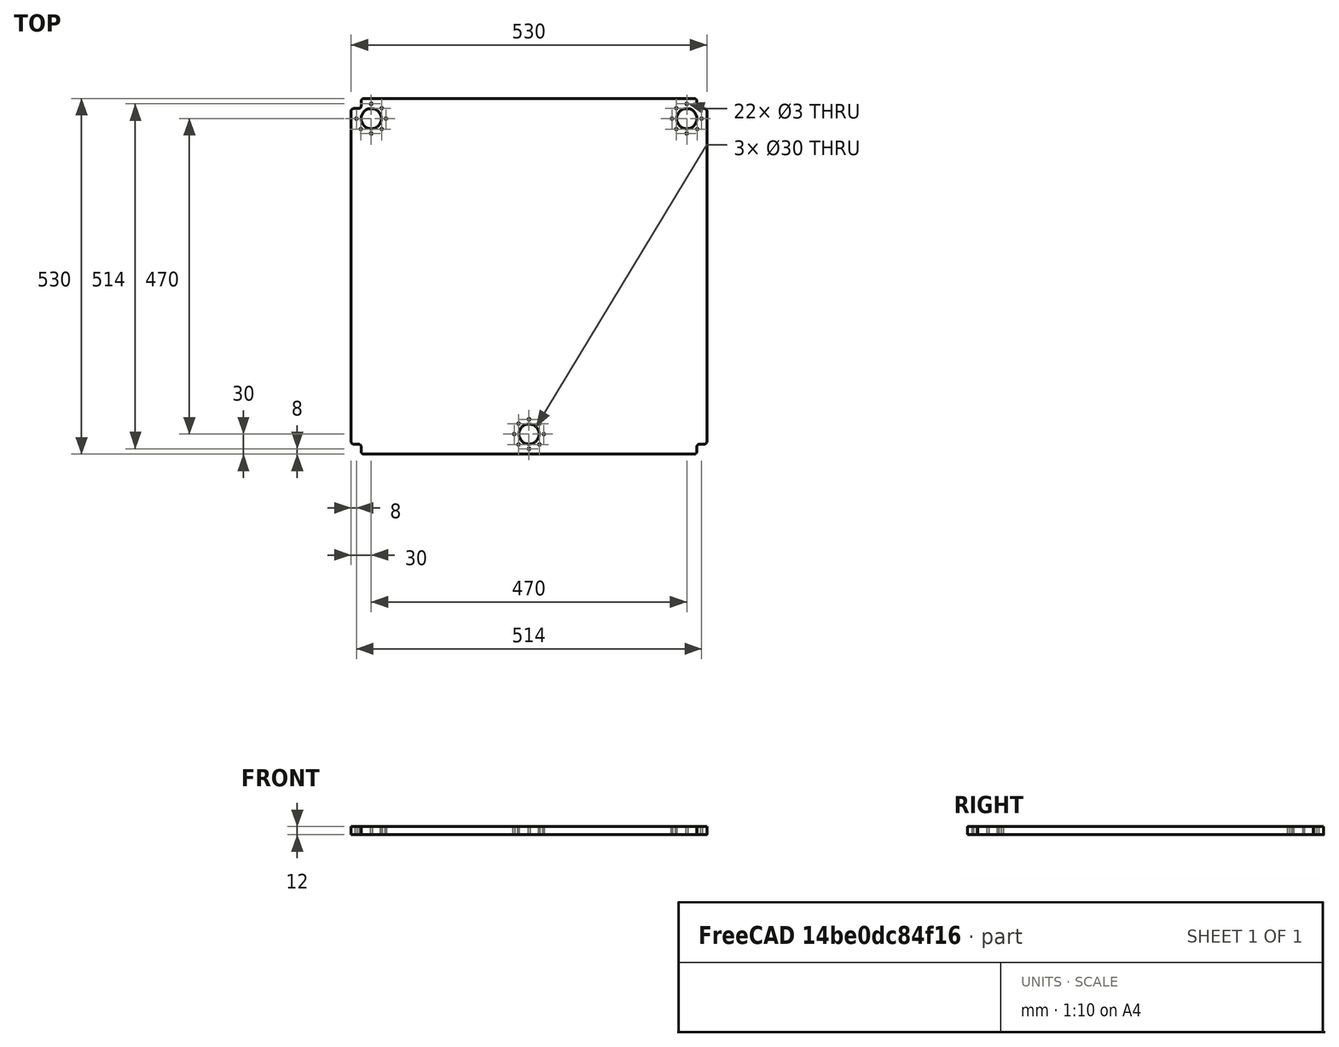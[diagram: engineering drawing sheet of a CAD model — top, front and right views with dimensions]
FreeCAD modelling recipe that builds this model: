
FCSTD DOCUMENT  (FreeCAD 0.19R)
Label: plateau_horizontal
License: All rights reserved
LicenseURL: http://en.wikipedia.org/wiki/All_rights_reserved
objects: TechDraw::DrawViewDimension×6, Sketcher::SketchObject×4, PartDesign::Pocket×3, PartDesign::Line×3, PartDesign::PolarPattern×3, TechDraw::DrawSVGTemplate×2, TechDraw::DrawPage×2, PartDesign::Pad×1, PartDesign::CoordinateSystem×1, PartDesign::Body×1, TechDraw::DrawViewPart×1
note: 20 computed .brp shape members not serialized (recipe doc carries the construction recipe); baked Part::Feature solids carry a one-line shape summary decoded from their .brp

FEATURE [Sketcher::SketchObject] Sketch
  FullyConstrained = true
  MapMode = 5
  Support = -> [XY_Plane]
  sketch-geometry (27):
    g0: Circle CenterX=0 CenterY=-235 CenterZ=0 NormalX=0 NormalY=0 NormalZ=1 AngleXU=0 Radius=15
    g1: Circle CenterX=-235 CenterY=235 CenterZ=0 NormalX=0 NormalY=0 NormalZ=1 AngleXU=0 Radius=15
    g2: Circle CenterX=235 CenterY=235 CenterZ=0 NormalX=0 NormalY=0 NormalZ=1 AngleXU=0 Radius=15
    g3: LineSegment StartX=-261 StartY=250 StartZ=0 EndX=-254 EndY=250 EndZ=0
    g4: LineSegment StartX=-250 StartY=254 StartZ=0 EndX=-250 EndY=261 EndZ=0
    g5: LineSegment StartX=-246 StartY=265 StartZ=0 EndX=246 EndY=265 EndZ=0
    g6: LineSegment StartX=250 StartY=261 StartZ=0 EndX=250 EndY=254 EndZ=0
    g7: LineSegment StartX=254 StartY=250 StartZ=0 EndX=261 EndY=250 EndZ=0
    g8: LineSegment StartX=265 StartY=246 StartZ=0 EndX=265 EndY=-246 EndZ=0
    g9: LineSegment StartX=261 StartY=-250 StartZ=0 EndX=254 EndY=-250 EndZ=0
    g10: LineSegment StartX=250 StartY=-254 StartZ=0 EndX=250 EndY=-261 EndZ=0
    g11: LineSegment StartX=246 StartY=-265 StartZ=0 EndX=-246 EndY=-265 EndZ=0
    g12: LineSegment StartX=-250 StartY=-261 StartZ=0 EndX=-250 EndY=-254 EndZ=0
    g13: LineSegment StartX=-254 StartY=-250 StartZ=0 EndX=-261 EndY=-250 EndZ=0
    g14: LineSegment StartX=-265 StartY=-246 StartZ=0 EndX=-265 EndY=246 EndZ=0
    g15: ArcOfCircle CenterX=-246 CenterY=261 CenterZ=0 NormalX=0 NormalY=0 NormalZ=1 AngleXU=0 Radius=4 StartAngle=1.5708 EndAngle=3.14159
    g16: ArcOfCircle CenterX=-254 CenterY=254 CenterZ=0 NormalX=0 NormalY=0 NormalZ=1 AngleXU=0 Radius=4 StartAngle=4.71239 EndAngle=6.28319
    g17: ArcOfCircle CenterX=-261 CenterY=246 CenterZ=0 NormalX=0 NormalY=0 NormalZ=1 AngleXU=0 Radius=4 StartAngle=1.5708 EndAngle=3.14159
    g18: ArcOfCircle CenterX=-261 CenterY=-246 CenterZ=0 NormalX=0 NormalY=0 NormalZ=1 AngleXU=0 Radius=4 StartAngle=3.14159 EndAngle=4.71239
    g19: ArcOfCircle CenterX=-254 CenterY=-254 CenterZ=0 NormalX=0 NormalY=0 NormalZ=1 AngleXU=0 Radius=4 StartAngle=1.5e-15 EndAngle=1.5708
    g20: ArcOfCircle CenterX=-246 CenterY=-261 CenterZ=0 NormalX=0 NormalY=0 NormalZ=1 AngleXU=0 Radius=4 StartAngle=3.14159 EndAngle=4.71239
    g21: ArcOfCircle CenterX=246 CenterY=-261 CenterZ=0 NormalX=0 NormalY=0 NormalZ=1 AngleXU=0 Radius=4 StartAngle=4.71239 EndAngle=6.28319
    g22: ArcOfCircle CenterX=254 CenterY=-254 CenterZ=0 NormalX=0 NormalY=0 NormalZ=1 AngleXU=0 Radius=4 StartAngle=1.5708 EndAngle=3.14159
    g23: ArcOfCircle CenterX=261 CenterY=-246 CenterZ=0 NormalX=0 NormalY=0 NormalZ=1 AngleXU=0 Radius=4 StartAngle=4.71239 EndAngle=6.28319
    g24: ArcOfCircle CenterX=261 CenterY=246 CenterZ=0 NormalX=0 NormalY=0 NormalZ=1 AngleXU=0 Radius=4 StartAngle=-1.8e-15 EndAngle=1.5708
    g25: ArcOfCircle CenterX=246 CenterY=261 CenterZ=0 NormalX=0 NormalY=0 NormalZ=1 AngleXU=0 Radius=4 StartAngle=-2.7e-15 EndAngle=1.5708
    g26: ArcOfCircle CenterX=254 CenterY=254 CenterZ=0 NormalX=0 NormalY=0 NormalZ=1 AngleXU=0 Radius=4 StartAngle=3.14159 EndAngle=4.71239
  constraints (62):
    c: PointOnObject(g0,g-2)
    c: Radius(g0) = 15
    c: Radius(g1) = 15
    c: Radius(g2) = 15
    c: Symmetric(g2,g1,g-2)
    c: Horizontal(g3)
    c: Vertical(g10)
    c: Horizontal(g11)
    c: Vertical(g12)
    c: Horizontal(g13)
    c: Vertical(g14)
    c: Tangent(g4,g15) = 1.5708
    c: Tangent(g5,g15) = 1.5708
    c: Tangent(g3,g16) = -1.5708
    c: Tangent(g4,g16) = -1.5708
    c: Tangent(g14,g17) = 1.5708
    c: Tangent(g3,g17) = 1.5708
    c: Tangent(g13,g18) = 1.5708
    c: Tangent(g14,g18) = 1.5708
    c: Tangent(g13,g19) = -1.5708
    c: Tangent(g12,g19) = -1.5708
    c: Tangent(g12,g20) = 1.5708
    c: Tangent(g11,g20) = 1.5708
    c: Tangent(g11,g21) = 1.5708
    c: Tangent(g10,g21) = 1.5708
    c: Tangent(g10,g22) = -1.5708
    c: Tangent(g9,g22) = -1.5708
    c: Tangent(g7,g24) = 1.5708
    c: Tangent(g8,g24) = 1.5708
    c: Tangent(g5,g25) = 1.5708
    c: Tangent(g6,g25) = 1.5708
    c: Tangent(g7,g26) = -1.5708
    c: Tangent(g6,g26) = -1.5708
    c: Symmetric(g5,g5,g-2)
    c: Symmetric(g4,g6,g-2)
    c: Symmetric(g7,g3,g-2)
    c: Symmetric(g7,g3,g-2)
    c: Vertical(g6)
    c: DistanceY(g0,g-1) = 235
    c: DistanceX(g1,g2) = 470
    c: DistanceY(g-1,g1) = 235
    c: DistanceY(g7,g5) = 15
    c: DistanceY(g-1,g7) = 250
    c: DistanceX(g-1,g6) = 250
    c: DistanceX(g6,g8) = 15
    c: Symmetric(g4,g12,g-1)
    c: Symmetric(g11,g5,g-1)
    c: Tangent(g23,g9) = 1.5708
    c: Tangent(g8,g23) = 1.5708
    c: Horizontal(g9)
    c: Vertical(g8)
    c: Radius(g22) = 4
    c: Radius(g21) = 4
    c: Radius(g23) = 4
    c: Radius(g18) = 4
    c: Radius(g19) = 4
    c: Radius(g20) = 4
    c: Radius(g24) = 4
    c: Radius(g26) = 4
    c: DistanceY(g11,g9) = 15
    c: DistanceX(g10,g8) = 15
    c: DistanceX(g14,g12) = 15
FEATURE [PartDesign::Pad] Pad
  Direction = (1,1,1)
  Length = 12
  Length2 = 100
  Profile = -> Sketch
  Type = 0
FEATURE [Sketcher::SketchObject] Sketch001
  ExternalGeometry = -> [Pad]
  FullyConstrained = true
  MapMode = 5
  Placement = pos=(0,0,12) rot=(0,0,1;0rad)
  Support = -> [Pad]
  sketch-geometry (2):
    g0: Circle CenterX=235 CenterY=257 CenterZ=0 NormalX=0 NormalY=0 NormalZ=1 AngleXU=0 Radius=1.5
    g1: LineSegment StartX=235 StartY=257 StartZ=0 EndX=235 EndY=235 EndZ=0
  constraints (5):
    c: Coincident(g1,g0)
    c: Coincident(g1,g-3)
    c: Vertical(g1)
    c: Radius(g0) = 1.5
    c: DistanceY(g1,g1) = 22
FEATURE [PartDesign::Pocket] Pocket
  BaseFeature = -> Pad
  Length = 5
  Length2 = 100
  Profile = -> Sketch001
  Type = 1
FEATURE [PartDesign::Line] DatumLine
  AttacherType = Attacher::AttachEngineLine
  Length = 20
  MapMode = 42
  Placement = pos=(235,235,0) rot=(0,0,1;0rad)
  ResizeMode = 0
  Support = -> [Pocket]
FEATURE [PartDesign::PolarPattern] PolarPattern
  Angle = 270
  Axis = -> DatumLine
  BaseFeature = -> Pocket
  Occurrences = 7
  Originals = -> [Pocket]
FEATURE [Sketcher::SketchObject] Sketch002
  ExternalGeometry = -> [PolarPattern]
  FullyConstrained = true
  MapMode = 5
  Placement = pos=(0,0,12) rot=(0,0,1;0rad)
  Support = -> [PolarPattern]
  sketch-geometry (2):
    g0: Circle CenterX=-235 CenterY=257 CenterZ=0 NormalX=0 NormalY=0 NormalZ=1 AngleXU=0 Radius=1.5
    g1: LineSegment StartX=-235 StartY=257 StartZ=0 EndX=-235 EndY=235 EndZ=0
  constraints (5):
    c: Coincident(g1,g0)
    c: Coincident(g1,g-3)
    c: Vertical(g1)
    c: Radius(g0) = 1.5
    c: DistanceY(g1,g1) = 22
FEATURE [PartDesign::Pocket] Pocket001
  BaseFeature = -> PolarPattern
  Length = 5
  Length2 = 100
  Profile = -> Sketch002
  Type = 1
FEATURE [PartDesign::Line] DatumLine001
  AttacherType = Attacher::AttachEngineLine
  Length = 20
  MapMode = 42
  Placement = pos=(-235,235,0) rot=(0,0,1;0rad)
  ResizeMode = 0
  Support = -> [Pocket001]
FEATURE [PartDesign::PolarPattern] PolarPattern001
  Angle = 270
  Axis = -> DatumLine001
  BaseFeature = -> Pocket001
  Occurrences = 7
  Originals = -> [Pocket001]
  Reversed = true
FEATURE [Sketcher::SketchObject] Sketch003
  ExternalGeometry = -> [PolarPattern001]
  FullyConstrained = true
  MapMode = 5
  Placement = pos=(0,0,12) rot=(0,0,1;0rad)
  Support = -> [PolarPattern001]
  sketch-geometry (1):
    g0: Circle CenterX=0 CenterY=-213 CenterZ=0 NormalX=0 NormalY=0 NormalZ=1 AngleXU=0 Radius=1.5
  constraints (3):
    c: PointOnObject(g0,g-2)
    c: DistanceY(g-3,g0) = 22
    c: Radius(g0) = 1.5
FEATURE [PartDesign::Pocket] Pocket002
  BaseFeature = -> PolarPattern001
  Length = 5
  Length2 = 100
  Profile = -> Sketch003
  Type = 1
FEATURE [PartDesign::Line] DatumLine002
  AttacherType = Attacher::AttachEngineLine
  Length = 20
  MapMode = 42
  Placement = pos=(1e-16,-235,0) rot=(0,0,1;0rad)
  ResizeMode = 0
  Support = -> [Pocket002]
FEATURE [PartDesign::PolarPattern] PolarPattern002
  Angle = 360
  Axis = -> DatumLine002
  BaseFeature = -> Pocket002
  Occurrences = 8
  Originals = -> [Pocket002]
FEATURE [PartDesign::CoordinateSystem] Local_CS
  AttacherType = Attacher::AttachEngine3D
  MapMode = 2
FEATURE [PartDesign::Body] Body
  Group = -> [Sketch,Pad,Sketch001,Pocket,DatumLine,PolarPattern,Sketch002,Pocket001,DatumLine001,PolarPattern001,Sketch003,Pocket002,DatumLine002,PolarPattern002,Local_CS]
  Origin = -> Origin
  Tip = -> PolarPattern002
FEATURE [TechDraw::DrawSVGTemplate] Template
  EditableTexts = Designed_by_Name=Designed by Name; Drawing_number=Drawing number; FC-Date=Date; FC-SC=Scale; FC-SH=Sheet; FC-Title=Title; Subtitle=Subtitle; Weight=Weight
  Height = 210
  Orientation = 1
  Width = 297
FEATURE [TechDraw::DrawViewPart] View
  CoarseView = false
  Direction = (0,0,1)
  Focus = 100
  HardHidden = false
  IsoCount = 0
  IsoHidden = false
  IsoVisible = false
  LockPosition = false
  Perspective = false
  Rotation = 0
  Scale = 0.2
  ScaleType = 0
  SeamHidden = false
  SeamVisible = true
  SmoothHidden = false
  SmoothVisible = true
  Source = -> [Body]
  X = 84.1
  XDirection = (1,0,0)
  Y = 133
FEATURE [TechDraw::DrawViewDimension] Dimension
  Arbitrary = false
  ArbitraryTolerances = false
  EqualTolerance = true
  FormatSpec = %.0f
  FormatSpecTolerance = %+.0f
  Inverted = false
  LockPosition = false
  MeasureType = 1
  OverTolerance = 0
  References2D = -> [View]
  Rotation = 0
  Scale = 0.2
  ScaleType = 0
  TheoreticalExact = false
  Type = 1
  UnderTolerance = 0
  X = -0.625143
  Y = -61.4843
FEATURE [TechDraw::DrawSVGTemplate] Template001
  EditableTexts = Designed_by_Name=Designed by Name; Drawing_number=Drawing number; FC-Date=Date; FC-SC=Scale; FC-SH=Sheet; FC-Title=Title; Subtitle=Subtitle; Weight=Weight
  Height = 210
  Orientation = 1
  Width = 297
FEATURE [TechDraw::DrawPage] Page001
  KeepUpdated = true
  NextBalloonIndex = 1
  ProjectionType = 0
  Template = -> Template001
FEATURE [TechDraw::DrawViewDimension] Dimension001
  Arbitrary = false
  ArbitraryTolerances = false
  EqualTolerance = true
  FormatSpec = %.0f
  FormatSpecTolerance = %+.0f
  Inverted = false
  LockPosition = false
  MeasureType = 1
  OverTolerance = 0
  References2D = -> [View]
  Rotation = 0
  Scale = 0.2
  ScaleType = 0
  TheoreticalExact = false
  Type = 1
  UnderTolerance = 0
  X = -2.81314
  Y = -54.8634
FEATURE [TechDraw::DrawViewDimension] Dimension002
  Arbitrary = false
  ArbitraryTolerances = false
  EqualTolerance = true
  FormatSpec = %.0f
  FormatSpecTolerance = %+.0f
  Inverted = false
  LockPosition = false
  MeasureType = 1
  OverTolerance = 0
  References2D = -> [View]
  Rotation = 0
  Scale = 0.2
  ScaleType = 0
  TheoreticalExact = false
  Type = 2
  UnderTolerance = 0
  X = 61.264
  Y = -34.4529
FEATURE [TechDraw::DrawViewDimension] Dimension003
  Arbitrary = false
  ArbitraryTolerances = false
  EqualTolerance = true
  FormatSpec = %.0f
  FormatSpecTolerance = %+.0f
  Inverted = false
  LockPosition = false
  MeasureType = 1
  OverTolerance = 0
  References2D = -> [View]
  Rotation = 0
  Scale = 0.2
  ScaleType = 0
  TheoreticalExact = false
  Type = 2
  UnderTolerance = 0
  X = 57.1057
  Y = 64.6369
FEATURE [TechDraw::DrawViewDimension] Dimension004
  Arbitrary = false
  ArbitraryTolerances = false
  EqualTolerance = true
  FormatSpec = %.0f
  FormatSpecTolerance = %+.0f
  Inverted = false
  LockPosition = false
  MeasureType = 1
  OverTolerance = 0
  References2D = -> [View]
  Rotation = 0
  Scale = 0.2
  ScaleType = 0
  TheoreticalExact = false
  Type = 2
  UnderTolerance = 0
  X = -45.0277
  Y = 63.5988
FEATURE [TechDraw::DrawViewDimension] Dimension005
  Arbitrary = false
  ArbitraryTolerances = false
  EqualTolerance = true
  FormatSpec = %.0f
  FormatSpecTolerance = %+.0f
  Inverted = false
  LockPosition = false
  MeasureType = 1
  OverTolerance = 0
  References2D = -> [View]
  Rotation = 0
  Scale = 0.2
  ScaleType = 0
  TheoreticalExact = false
  Type = 1
  UnderTolerance = 0
  X = -2.73924
  Y = 37.2415
FEATURE [TechDraw::DrawPage] Page
  KeepUpdated = true
  NextBalloonIndex = 1
  ProjectionType = 0
  Scale = 0.2
  Template = -> Template
  Views = -> [View,Dimension,Dimension001,Dimension002,Dimension003,Dimension004,Dimension005]
